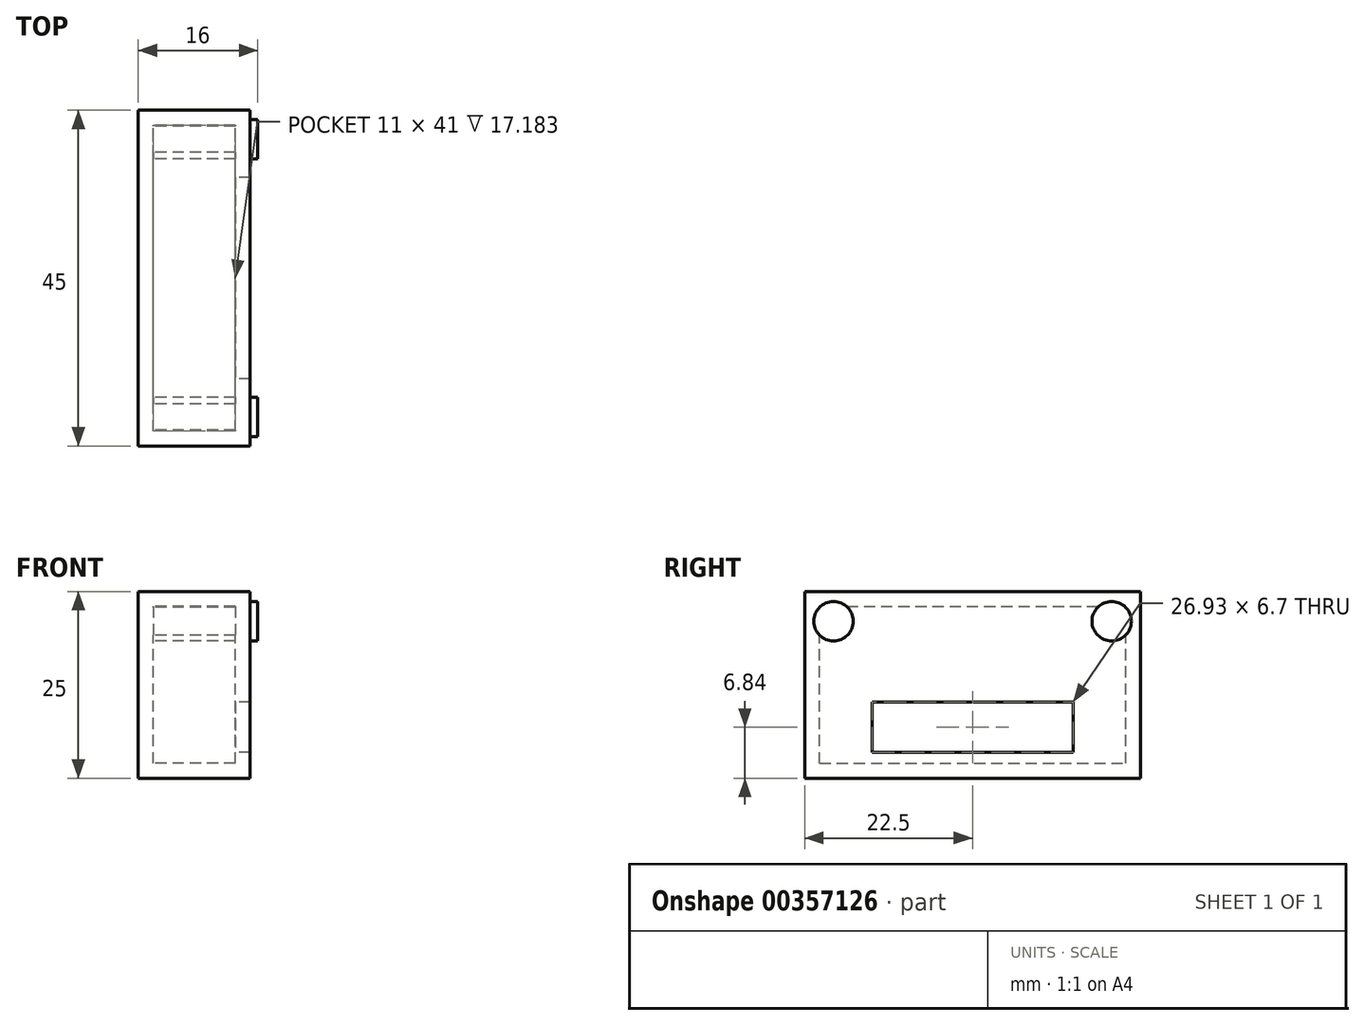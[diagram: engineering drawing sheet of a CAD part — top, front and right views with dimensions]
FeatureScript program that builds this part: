
annotation { "Feature Type Name" : "Feature", "Feature Type Description" : "" }
export const myFeature = defineFeature(function(context is Context, id is Id, definition is map)
    precondition{}
    {
        {
            var Q0;
            Q0=qCreatedBy(makeId("Right.planeOp"),FACE);
            var sketch = newSketch(context, id + "F0", { "sketchPlane" : qUnion([Q0])});
            skLineSegment(sketch, "E0.bottom", {"start": v(-22.5, -12.5) * mm, "end": v(22.5, -12.5) * mm});
            skLineSegment(sketch, "E0.top", {"start": v(-22.5, 12.5) * mm, "end": v(22.5, 12.5) * mm});
            skLineSegment(sketch, "E0.left", {"start": v(-22.5, -12.5) * mm, "end": v(-22.5, 12.5) * mm});
            skLineSegment(sketch, "E0.right", {"start": v(22.5, -12.5) * mm, "end": v(22.5, 12.5) * mm});
            skPoint(sketch, "E0.middle", {"position": v(0, 0) * mm});
            skSolve(sketch);
        }
        {
            var Q0;
            Q0 = qSketchRegion(id + "F0", true);
            extrude(context, id + "F1", {"entities" : qUnion([Q0]), "depth" : 15 * mm});
        }
        {
            var Q0;
            Q0=qCreatedBy(makeId("Right.planeOp"),FACE);
            var sketch = newSketch(context, id + "F2", { "sketchPlane" : qUnion([Q0])});
            skLineSegment(sketch, "E1.bottom", {"start": v(-13.47, -9.01) * mm, "end": v(13.47, -9.01) * mm});
            skLineSegment(sketch, "E1.top", {"start": v(-13.47, -2.3) * mm, "end": v(13.47, -2.3) * mm});
            skLineSegment(sketch, "E1.left", {"start": v(-13.47, -9.01) * mm, "end": v(-13.47, -2.3) * mm});
            skLineSegment(sketch, "E1.right", {"start": v(13.47, -9.01) * mm, "end": v(13.47, -2.3) * mm});
            skPoint(sketch, "E1.middle", {"position": v(0, -5.66) * mm});
            skLineSegment(sketch, "E2", {"start": v(-9.59, -2.3) * mm, "end": v(-9.59, -9.01) * mm});
            skLineSegment(sketch, "E3", {"start": v(-3.77, -2.3) * mm, "end": v(-3.77, -9.01) * mm});
            skLineSegment(sketch, "E4.MirrorCS", {"start": v(3.77, -2.3) * mm, "end": v(3.77, -9.01) * mm});
            skLineSegment(sketch, "E5.MirrorCS", {"start": v(9.59, -2.3) * mm, "end": v(9.59, -9.01) * mm});
            skSolve(sketch);
        }
        {
            var Q0;
            Q0 = qSketchRegion(id + "F2", true);
            extrude(context, id + "F3", {"entities" : qUnion([Q0]), "operationType" : NewBodyOperationType.ADD, "depth" : 25 * mm});
        }
        {
            var Q0;
            Q0=makeQuery(id+"F3.opExtrude","SWEPT_FACE",FACE,{"disambiguationData":[OSD([sQuery(id+"F2.wireOp",EDGE,"E1.left")])]});
            var Q1;
            Q1=makeQuery(id+"F3.opExtrude","SWEPT_FACE",FACE,{"disambiguationData":[OSD([sQuery(id+"F2.wireOp",EDGE,"E1.bottom")])]});
            var Q2;
            Q2=makeQuery(id+"F3.opExtrude","SWEPT_FACE",FACE,{"disambiguationData":[OSD([sQuery(id+"F2.wireOp",EDGE,"E1.right")])]});
            var Q3;
            Q3=makeQuery(id+"F3.opExtrude","CAP_FACE",FACE,{"disambiguationData":[OSD([sQuery(id+"F2.wireOp",EDGE,"E1.bottom"),sQuery(id+"F2.wireOp",EDGE,"E1.top"),sQuery(id+"F2.wireOp",EDGE,"E1.left"),sQuery(id+"F2.wireOp",EDGE,"E1.right")])],"isStart":false});
            var Q4;
            Q4=makeQuery(id+"F3.opExtrude","SWEPT_FACE",FACE,{"disambiguationData":[OSD([sQuery(id+"F2.wireOp",EDGE,"E1.top")])]});
            shell(context, id + "F4", {"entities" : qUnion([Q0, Q1, Q2, Q3, Q4]), "thickness" : 2 * mm});
        }
        {
            var Q0;
            Q0=qCreatedBy(makeId("Right.planeOp"),FACE);
            var sketch = newSketch(context, id + "F5", { "sketchPlane" : qUnion([Q0])});
            skCircle(sketch, "E6", {"center": v(-18.62, 8.53) * mm, "radius": 2.64 * mm});
            skCircle(sketch, "E7.MirrorC", {"center": v(18.62, 8.53) * mm, "radius": 2.64 * mm});
            skSolve(sketch);
        }
        {
            var Q0;
            Q0 = qSketchRegion(id + "F5", true);
            extrude(context, id + "F6", {"entities" : qUnion([Q0]), "operationType" : NewBodyOperationType.ADD, "depth" : 5 * mm});
        }
        {
            var Q0;
            Q0 = qSketchRegion(id + "F5", true);
            extrude(context, id + "F7", {"entities" : qUnion([Q0]), "operationType" : NewBodyOperationType.ADD, "depth" : 16 * mm});
        }
    });
